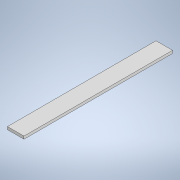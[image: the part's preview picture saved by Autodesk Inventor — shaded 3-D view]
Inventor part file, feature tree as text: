
AUTODESK INVENTOR PART (.ipt)
format: ipt  version: 2022 (Build 260153000, 153)  size: 104,448 bytes
history: native  units: mm
features: sketch x2, other x1, extrude x1, hole x1
ambient origin geometry x8: Origin, YZ Plane, XZ Plane, XY Plane, X Axis, Y Axis, Z Axis, Center Point
bodies: Body1 (feature_tree), Body2 (feature_tree)
feature tree (5):
  other  "ソリッド1"
  extrude  "押し出し1"  Depth=270.0mm
  hole  "穴1"  [1 undecoded]
  sketch  "スケッチ1"
  sketch  "スケッチ2"
note: 1 required parameter value undecoded (feature->parameter linkage not recoverable at this tier; creation-order binding heuristic only, values carry confidence <= 0.55)
